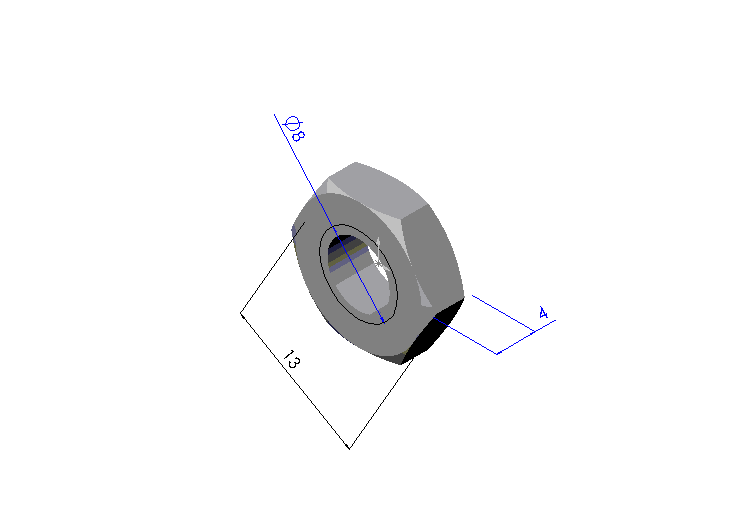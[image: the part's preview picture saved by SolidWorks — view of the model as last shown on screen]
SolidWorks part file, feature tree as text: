
SOLIDWORKS PART (.sldprt)
format: sldprt  version: not decoded by parser v0  size: 143,360 bytes
history: native  units: mm
features: plane x3, sketch x3, material x1, extrude x1, mirror x1, cut_extrude x1, thread x1 (+8 scaffold rows collapsed)
feature tree (19):
  scaffold x8  (default folders/planes/origin — collapsed)
  material  "Matériau <non spécifié>"
  plane  "Plan1"
  plane  "Plan2"
  plane  "Plan3"
  sketch  "Esquisse1"  dims[c1.D1=10.0mm c2.D1=60.0deg c2.D2=10.0mm c3.D2=60.0deg c3.D3=~13.660254mm c4.D3=60.0deg c4.D4=~13.660254mm c5.D4=60.0deg c5.D5=15.0mm c5.D1=~28.284271mm c6.D1=60.0deg c6.D2=~28.284271mm c7.D2=30.0deg c8.D2=~36.055513mm c9.D2=60.0deg c9.D1=~36.055513mm c10.D1=60.0deg c10.D2=~36.055513mm c11.D2=60.0deg c11.D3=13.0mm c11.D4=30.0mm c12.D4=10.0deg]
  extrude  "Base-Extrusion"  Depth=4mm
  sketch  "Esquisse5"  dims[c1.D1=6.8mm c2.D1=60.0deg c3.D1=360.0deg c3.D3=1.0mm c3.D4=1.0mm c3.D7=0.0mm]
  mirror  "Symétrie1"
  sketch  "Esquisse4"  dims[D1=6.4mm]
  cut_extrude  "Enlèv. mat.-Extru.1"  [1 undecoded]
  thread  "Représentation de filetage1"  Diameter=8mm  [1 undecoded]
decode coverage: 5 of 7 modeling features carry decoded parameters
note: ~ marks probable driven/reference dimensions
note: 2 parameter values undecoded
note: suppression state not decoded; provenance and decode notes live in map.json
